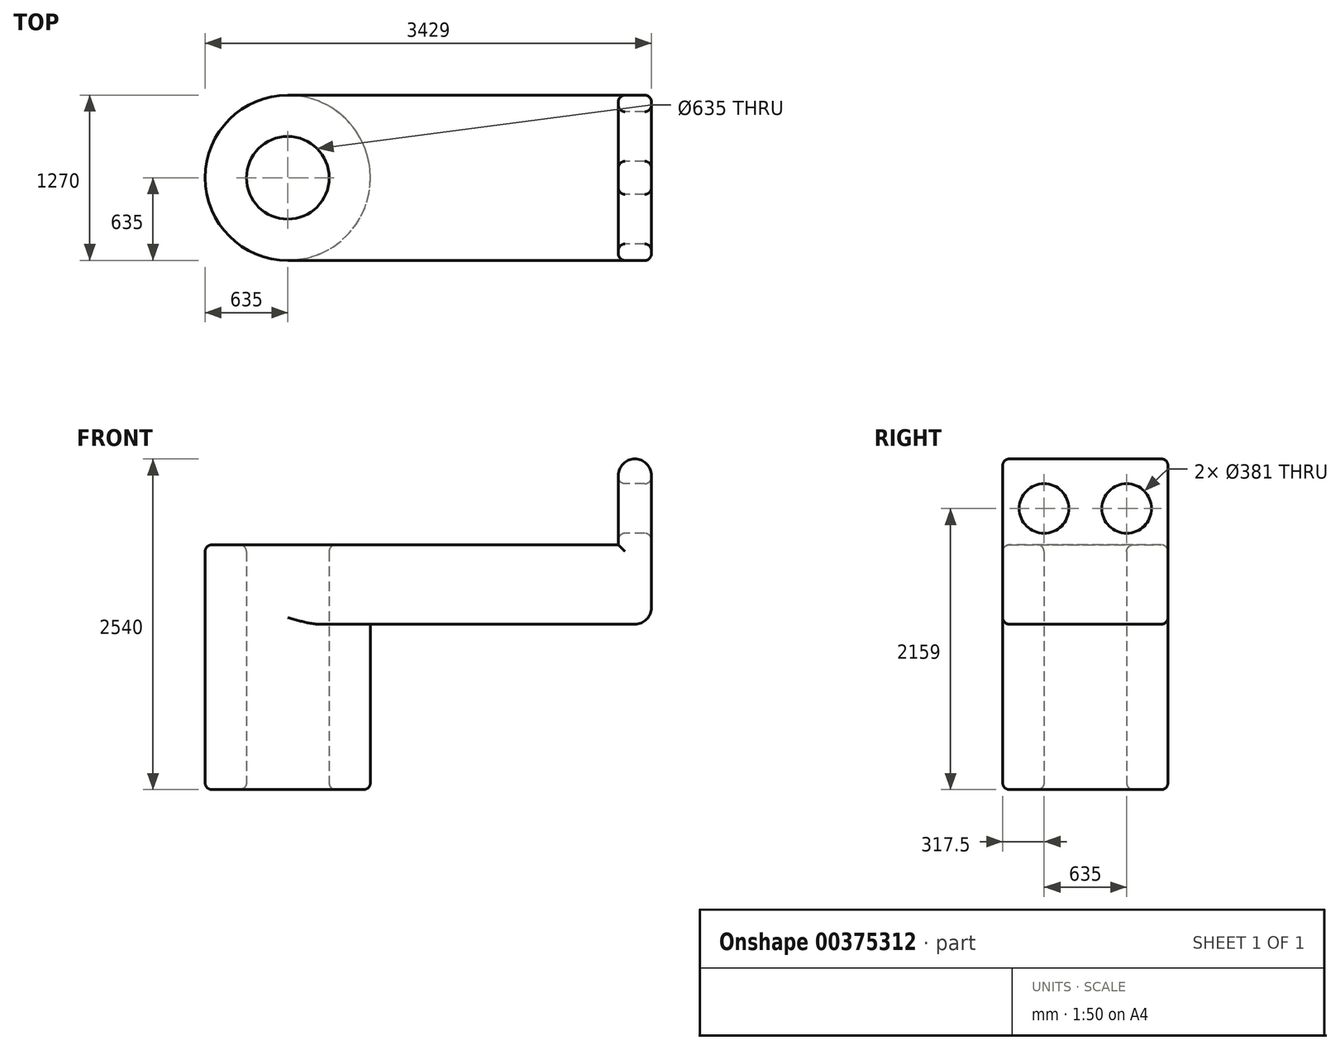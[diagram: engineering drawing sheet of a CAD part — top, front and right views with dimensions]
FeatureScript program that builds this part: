
annotation { "Feature Type Name" : "Feature", "Feature Type Description" : "" }
export const myFeature = defineFeature(function(context is Context, id is Id, definition is map)
    precondition{}
    {
        {
            var Q0;
            Q0=qCreatedBy(makeId("Top.planeOp"),FACE);
            var sketch = newSketch(context, id + "F0", { "sketchPlane" : qUnion([Q0])});
            skLineSegment(sketch, "E0.bottom", {"start": v(-1270, -635) * mm, "end": v(1270, -635) * mm});
            skLineSegment(sketch, "E0.top", {"start": v(-1270, 635) * mm, "end": v(1270, 635) * mm});
            skLineSegment(sketch, "E0.left", {"start": v(-1270, -635) * mm, "end": v(-1270, 635) * mm});
            skLineSegment(sketch, "E0.right", {"start": v(1270, -635) * mm, "end": v(1270, 635) * mm});
            skPoint(sketch, "E0.middle", {"position": v(0, 0) * mm});
            skCircle(sketch, "E1", {"center": v(-1270, 0) * mm, "radius": 635 * mm});
            skCircle(sketch, "E2", {"center": v(-1270, 0) * mm, "radius": 317.5 * mm});
            skSolve(sketch);
        }
        {
            var Q0;
            Q0 = qSketchRegion(id + "F0", true);
            extrude(context, id + "F1", {"entities" : qUnion([Q0]), "depth" : 609.6 * mm});
        }
        {
            var Q0;
            {var subQ1=sQuery(id+"F0.wireOp",EDGE,"E0.left");var subQ3=sQuery(id+"F0.wireOp",EDGE,"E2");var subQ4=makeQuery(id+"F0.imprint","INTERSECT",VERTEX,{"disambiguationData":[OD(0.0)],"derivedFrom":[subQ1,subQ3]});Q0=makeQuery(id+"F0.imprint","IMPRINT",FACE,{"disambiguationData":[TD([[makeQuery(id+"F0.imprint","IMPRINT",EDGE,{"disambiguationData":[TD([[subQ4,1.0]])],"derivedFrom":subQ3}),-1.0]])]});}
            var Q1;
            {var subQ1=sQuery(id+"F0.wireOp",EDGE,"E0.left");var subQ3=sQuery(id+"F0.wireOp",EDGE,"E2");var subQ4=makeQuery(id+"F0.imprint","INTERSECT",VERTEX,{"disambiguationData":[OD(0.0)],"derivedFrom":[subQ1,subQ3]});Q1=makeQuery(id+"F0.imprint","IMPRINT",FACE,{"disambiguationData":[TD([[makeQuery(id+"F0.imprint","IMPRINT",EDGE,{"disambiguationData":[TD([[subQ4,-1.0]])],"derivedFrom":subQ3}),-1.0]])]});}
            extrude(context, id + "F2", {"entities" : qUnion([Q0, Q1]), "operationType" : NewBodyOperationType.ADD, "oppositeDirection" : true, "depth" : 1270 * mm});
        }
        {
            var Q0;
            Q0=makeQuery(id+"F1.opExtrude","SWEPT_FACE",FACE,{"disambiguationData":[OSD([sQuery(id+"F0.wireOp",EDGE,"E0.right")])]});
            var sketch = newSketch(context, id + "F3", { "sketchPlane" : qUnion([Q0])});
            skLineSegment(sketch, "E3.bottom", {"start": v(635, 0) * mm, "end": v(-635, 0) * mm});
            skLineSegment(sketch, "E3.top", {"start": v(635, 1270) * mm, "end": v(-635, 1270) * mm});
            skLineSegment(sketch, "E3.left", {"start": v(635, 0) * mm, "end": v(635, 1270) * mm});
            skLineSegment(sketch, "E3.right", {"start": v(-635, 0) * mm, "end": v(-635, 1270) * mm});
            skLineSegment(sketch, "E4", {"start": v(0, 1411.4) * mm, "end": v(0, -344.7) * mm, "construction": true});
            skPoint(sketch, "E4.startSnap0", {"position": v(0, 0) * mm});
            skPoint(sketch, "E4.endSnap0", {"position": v(0, 609.6) * mm});
            skCircle(sketch, "E5", {"center": v(-317.5, 889) * mm, "radius": 190.5 * mm});
            skCircle(sketch, "E6.MirrorC", {"center": v(317.5, 889) * mm, "radius": 190.5 * mm});
            skSolve(sketch);
        }
        {
            var Q0;
            Q0 = qSketchRegion(id + "F3", true);
            extrude(context, id + "F4", {"entities" : qUnion([Q0]), "operationType" : NewBodyOperationType.ADD, "depth" : 254 * mm});
        }
        {
            var Q0;
            Q0=makeQuery(id+"F2.opExtrude","CAP_EDGE",EDGE,{"disambiguationData":[OSD([sQuery(id+"F0.wireOp",EDGE,"E1")])],"isStart":true});
            var Q1;
            Q1=makeQuery(id+"F4.opExtrude","CAP_EDGE",EDGE,{"disambiguationData":[OSD([sQuery(id+"F3.wireOp",EDGE,"E3.bottom")])],"isStart":false});
            var Q2;
            Q2=makeQuery(id+"F4.opExtrude","CAP_EDGE",EDGE,{"disambiguationData":[OSD([sQuery(id+"F3.wireOp",EDGE,"E3.top")])],"isStart":false});
            var Q3;
            Q3=makeQuery(id+"F4.opExtrude","CAP_EDGE",EDGE,{"disambiguationData":[OSD([sQuery(id+"F3.wireOp",EDGE,"E3.top")])],"isStart":true});
            fillet(context, id + "F5", {"entities" : qUnion([Q0, Q1, Q2, Q3]), "radius" : 127 * mm, "tangentPropagation" : true, "allowEdgeOverflow" : false});
        }
        {
            var Q0;
            Q0=makeQuery(id+"F4.boolean.opBoolean","MERGE",EDGE,{"derivedFrom":[makeQuery(id+"F1.opExtrude","CAP_EDGE",EDGE,{"disambiguationData":[OSD([sQuery(id+"F0.wireOp",EDGE,"E0.top")])],"isStart":true}),makeQuery(id+"F4.opExtrude","SWEPT_EDGE",EDGE,{"disambiguationData":[OSD([sQuery(id+"F3.wireOp",EDGE,"E3.bottom"),sQuery(id+"F3.wireOp",EDGE,"E3.left")])]})]});
            var Q1;
            Q1=makeQuery(id+"F4.boolean.opBoolean","MERGE",EDGE,{"derivedFrom":[makeQuery(id+"F1.opExtrude","CAP_EDGE",EDGE,{"disambiguationData":[OSD([sQuery(id+"F0.wireOp",EDGE,"E0.bottom")])],"isStart":true}),makeQuery(id+"F4.opExtrude","SWEPT_EDGE",EDGE,{"disambiguationData":[OSD([sQuery(id+"F3.wireOp",EDGE,"E3.bottom"),sQuery(id+"F3.wireOp",EDGE,"E3.right")])]})]});
            var Q2;
            Q2=makeQuery(id+"F1.opExtrude","CAP_EDGE",EDGE,{"disambiguationData":[OSD([sQuery(id+"F0.wireOp",EDGE,"E0.top")])],"isStart":false});
            var Q3;
            Q3=makeQuery(id+"F2.opExtrude","CAP_EDGE",EDGE,{"disambiguationData":[OSD([sQuery(id+"F0.wireOp",EDGE,"E1")])],"isStart":false});
            var Q4;
            Q4=makeQuery(id+"F2.opExtrude","CAP_EDGE",EDGE,{"disambiguationData":[OSD([sQuery(id+"F0.wireOp",EDGE,"E2")])],"isStart":false});
            var Q5;
            Q5=makeQuery(id+"F1.opExtrude","CAP_EDGE",EDGE,{"disambiguationData":[OSD([sQuery(id+"F0.wireOp",EDGE,"E2")])],"isStart":false});
            var Q6;
            Q6=makeQuery(id+"F4.opExtrude","CAP_EDGE",EDGE,{"disambiguationData":[OSD([sQuery(id+"F3.wireOp",EDGE,"E5")])],"isStart":false});
            var Q7;
            Q7=makeQuery(id+"F4.opExtrude","CAP_EDGE",EDGE,{"disambiguationData":[OSD([sQuery(id+"F3.wireOp",EDGE,"E6.MirrorC")])],"isStart":true});
            var Q8;
            Q8=makeQuery(id+"F4.opExtrude","CAP_EDGE",EDGE,{"disambiguationData":[OSD([sQuery(id+"F3.wireOp",EDGE,"E5")])],"isStart":true});
            var Q9;
            Q9=makeQuery(id+"F4.opExtrude","CAP_EDGE",EDGE,{"disambiguationData":[OSD([sQuery(id+"F3.wireOp",EDGE,"E6.MirrorC")])],"isStart":false});
            fillet(context, id + "F6", {"entities" : qUnion([Q0, Q1, Q2, Q3, Q4, Q5, Q6, Q7, Q8, Q9]), "radius" : 50.8 * mm, "tangentPropagation" : true, "allowEdgeOverflow" : false});
        }
    });
